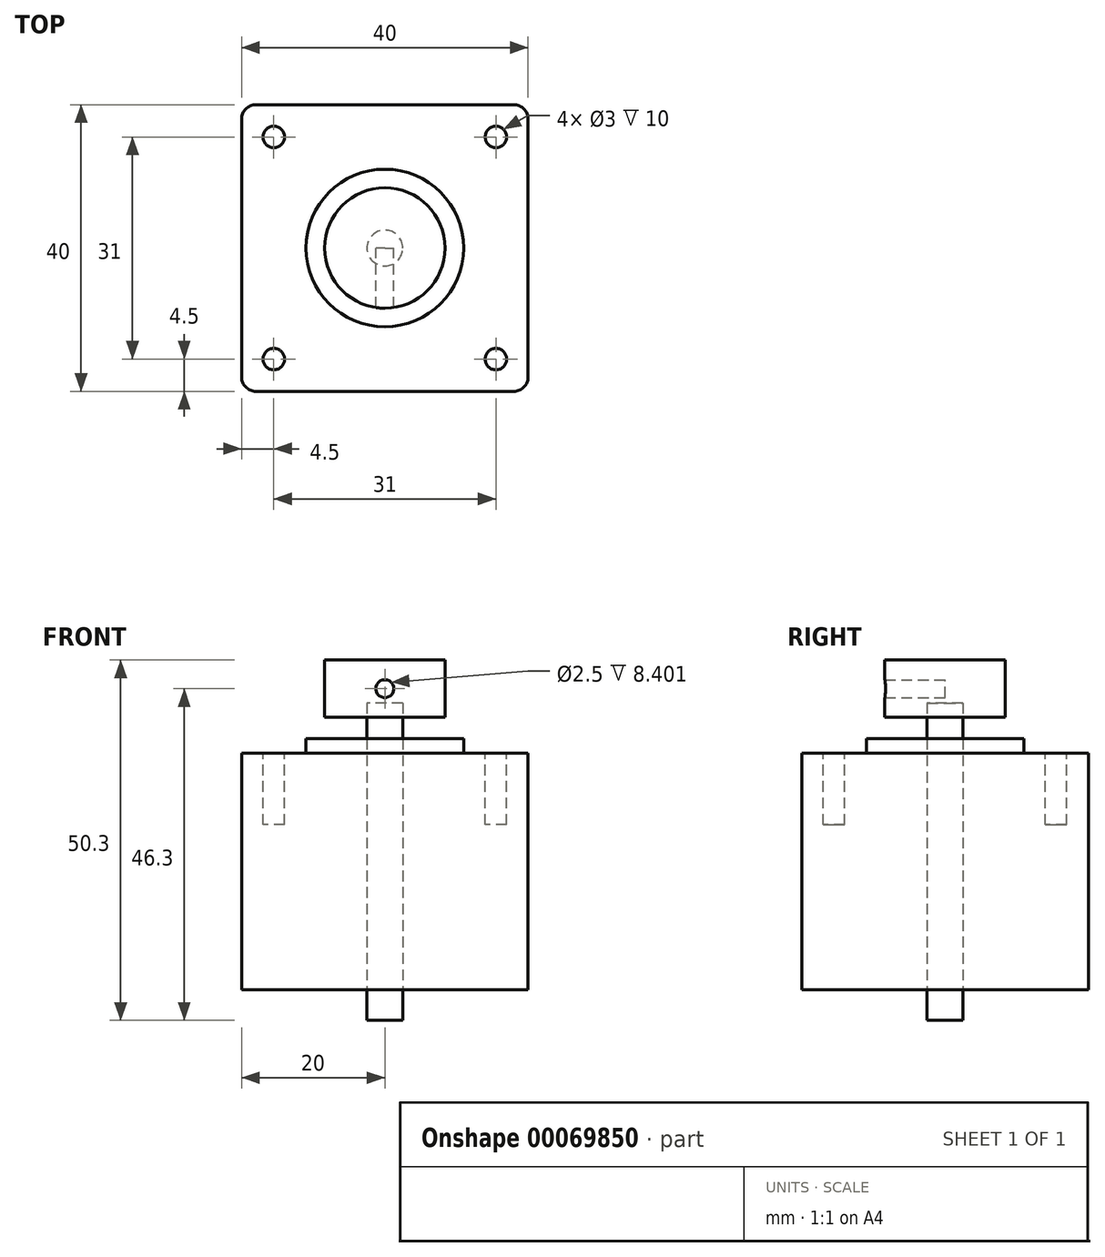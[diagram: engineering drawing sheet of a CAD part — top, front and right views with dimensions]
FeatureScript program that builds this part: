
annotation { "Feature Type Name" : "Feature", "Feature Type Description" : "" }
export const myFeature = defineFeature(function(context is Context, id is Id, definition is map)
    precondition{}
    {
        {
            var Q0;
            Q0=qCreatedBy(makeId("Top.planeOp"),FACE);
            var sketch = newSketch(context, id + "F0", { "sketchPlane" : qUnion([Q0])});
            skLineSegment(sketch, "E0.rect.bottom", {"start": v(18, 20) * mm, "end": v(-18, 20) * mm});
            skLineSegment(sketch, "E0.rect.top", {"start": v(18, -20) * mm, "end": v(-18, -20) * mm});
            skLineSegment(sketch, "E0.rect.left", {"start": v(20, 18) * mm, "end": v(20, -18) * mm});
            skLineSegment(sketch, "E0.rect.right", {"start": v(-20, 18) * mm, "end": v(-20, -18) * mm});
            skPoint(sketch, "E0.rect.middle", {"position": v(0, 0) * mm});
            skPoint(sketch, "E1.visualSharp", {"position": v(20, 20) * mm});
            skArc(sketch, "E1.filletArc", {"start": v(20, 18) * mm, "mid": v(19.41, 19.41) * mm, "end": v(18, 20) * mm});
            skPoint(sketch, "E2.visualSharp", {"position": v(-20, 20) * mm});
            skArc(sketch, "E2.filletArc", {"start": v(-18, 20) * mm, "mid": v(-19.41, 19.41) * mm, "end": v(-20, 18) * mm});
            skPoint(sketch, "E3.visualSharp", {"position": v(-20, -20) * mm});
            skArc(sketch, "E3.filletArc", {"start": v(-20, -18) * mm, "mid": v(-19.41, -19.41) * mm, "end": v(-18, -20) * mm});
            skPoint(sketch, "E4.visualSharp", {"position": v(20, -20) * mm});
            skArc(sketch, "E4.filletArc", {"start": v(18, -20) * mm, "mid": v(19.41, -19.41) * mm, "end": v(20, -18) * mm});
            skSolve(sketch);
        }
        {
            var Q0;
            Q0 = qSketchRegion(id + "F0", true);
            extrude(context, id + "F1", {"entities" : qUnion([Q0]), "depth" : 33 * mm});
        }
        {
            var Q0;
            Q0=makeQuery(id+"F1.opExtrude","CAP_FACE",FACE,{"disambiguationData":[OSD([sQuery(id+"F0.wireOp",EDGE,"E0.rect.bottom"),sQuery(id+"F0.wireOp",EDGE,"E0.rect.top"),sQuery(id+"F0.wireOp",EDGE,"E0.rect.left"),sQuery(id+"F0.wireOp",EDGE,"E0.rect.right"),sQuery(id+"F0.wireOp",EDGE,"E1.filletArc"),sQuery(id+"F0.wireOp",EDGE,"E2.filletArc"),sQuery(id+"F0.wireOp",EDGE,"E3.filletArc"),sQuery(id+"F0.wireOp",EDGE,"E4.filletArc")])],"isStart":false});
            var sketch = newSketch(context, id + "F2", { "sketchPlane" : qUnion([Q0])});
            skCircle(sketch, "E5", {"center": v(0, 0) * mm, "radius": 11 * mm});
            skSolve(sketch);
        }
        {
            var Q0;
            Q0 = qSketchRegion(id + "F2", true);
            extrude(context, id + "F3", {"entities" : qUnion([Q0]), "operationType" : NewBodyOperationType.ADD, "depth" : 2 * mm});
        }
        {
            var Q0;
            Q0=makeQuery(id+"F1.opExtrude","CAP_FACE",FACE,{"disambiguationData":[OSD([sQuery(id+"F0.wireOp",EDGE,"E0.rect.bottom"),sQuery(id+"F0.wireOp",EDGE,"E0.rect.top"),sQuery(id+"F0.wireOp",EDGE,"E0.rect.left"),sQuery(id+"F0.wireOp",EDGE,"E0.rect.right"),sQuery(id+"F0.wireOp",EDGE,"E1.filletArc"),sQuery(id+"F0.wireOp",EDGE,"E2.filletArc"),sQuery(id+"F0.wireOp",EDGE,"E3.filletArc"),sQuery(id+"F0.wireOp",EDGE,"E4.filletArc")])],"isStart":false});
            var sketch = newSketch(context, id + "F4", { "sketchPlane" : qUnion([Q0])});
            skCircle(sketch, "E6", {"center": v(0, 0) * mm, "radius": 8.4 * mm});
            skSolve(sketch);
        }
        {
            var Q0;
            Q0 = qSketchRegion(id + "F4", true);
            extrude(context, id + "F5", {"entities" : qUnion([Q0]), "depth" : 13 * mm, "hasSecondDirection" : true, "secondDirectionOppositeDirection" : false, "secondDirectionDepth" : (13 - 8) * mm});
        }
        {
            var Q0;
            Q0=qCreatedBy(makeId("Top.planeOp"),FACE);
            var sketch = newSketch(context, id + "F6", { "sketchPlane" : qUnion([Q0])});
            skCircle(sketch, "E7", {"center": v(0, 0) * mm, "radius": 2.5 * mm});
            skSolve(sketch);
        }
        {
            var Q0;
            Q0 = qSketchRegion(id + "F6", true);
            extrude(context, id + "F7", {"entities" : qUnion([Q0]), "depth" : 40 * mm, "hasSecondDirection" : true, "secondDirectionOppositeDirection" : true, "secondDirectionDepth" : 4.3 * mm});
        }
        {
            var Q0;
            Q0=makeQuery(id+"F1.opExtrude","CAP_FACE",FACE,{"disambiguationData":[OSD([sQuery(id+"F0.wireOp",EDGE,"E0.rect.bottom"),sQuery(id+"F0.wireOp",EDGE,"E0.rect.top"),sQuery(id+"F0.wireOp",EDGE,"E0.rect.left"),sQuery(id+"F0.wireOp",EDGE,"E0.rect.right"),sQuery(id+"F0.wireOp",EDGE,"E1.filletArc"),sQuery(id+"F0.wireOp",EDGE,"E2.filletArc"),sQuery(id+"F0.wireOp",EDGE,"E3.filletArc"),sQuery(id+"F0.wireOp",EDGE,"E4.filletArc")])],"isStart":false});
            var sketch = newSketch(context, id + "F8", { "sketchPlane" : qUnion([Q0])});
            skLineSegment(sketch, "E8.rect.bottom", {"start": v(15.5, 15.5) * mm, "end": v(-15.5, 15.5) * mm, "construction": true});
            skLineSegment(sketch, "E8.rect.top", {"start": v(15.5, -15.5) * mm, "end": v(-15.5, -15.5) * mm, "construction": true});
            skLineSegment(sketch, "E8.rect.left", {"start": v(15.5, 15.5) * mm, "end": v(15.5, -15.5) * mm, "construction": true});
            skLineSegment(sketch, "E8.rect.right", {"start": v(-15.5, 15.5) * mm, "end": v(-15.5, -15.5) * mm, "construction": true});
            skPoint(sketch, "E8.rect.middle", {"position": v(0, 0) * mm});
            skCircle(sketch, "E9", {"center": v(15.5, 15.5) * mm, "radius": 1.5 * mm});
            skCircle(sketch, "E10", {"center": v(-15.5, 15.5) * mm, "radius": 1.5 * mm});
            skCircle(sketch, "E11", {"center": v(-15.5, -15.5) * mm, "radius": 1.5 * mm});
            skCircle(sketch, "E12", {"center": v(15.5, -15.5) * mm, "radius": 1.5 * mm});
            skSolve(sketch);
        }
        {
            var Q0;
            Q0 = qSketchRegion(id + "F8", true);
            extrude(context, id + "F9", {"entities" : qUnion([Q0]), "operationType" : NewBodyOperationType.REMOVE, "oppositeDirection" : true, "depth" : 10 * mm});
        }
        {
            var Q0;
            Q0=qCreatedBy(makeId("Front.planeOp"),FACE);
            var sketch = newSketch(context, id + "F10", { "sketchPlane" : qUnion([Q0])});
            skLineSegment(sketch, "E13", {"start": v(0, 46) * mm, "end": v(0, 38) * mm, "construction": true});
            skCircle(sketch, "E14", {"center": v(0, 42) * mm, "radius": 1.25 * mm});
            skSolve(sketch);
        }
        {
            var Q0;
            Q0 = qSketchRegion(id + "F10", true);
            extrude(context, id + "F11", {"entities" : qUnion([Q0]), "operationType" : NewBodyOperationType.REMOVE, "depth" : 25 * mm});
        }
    });
